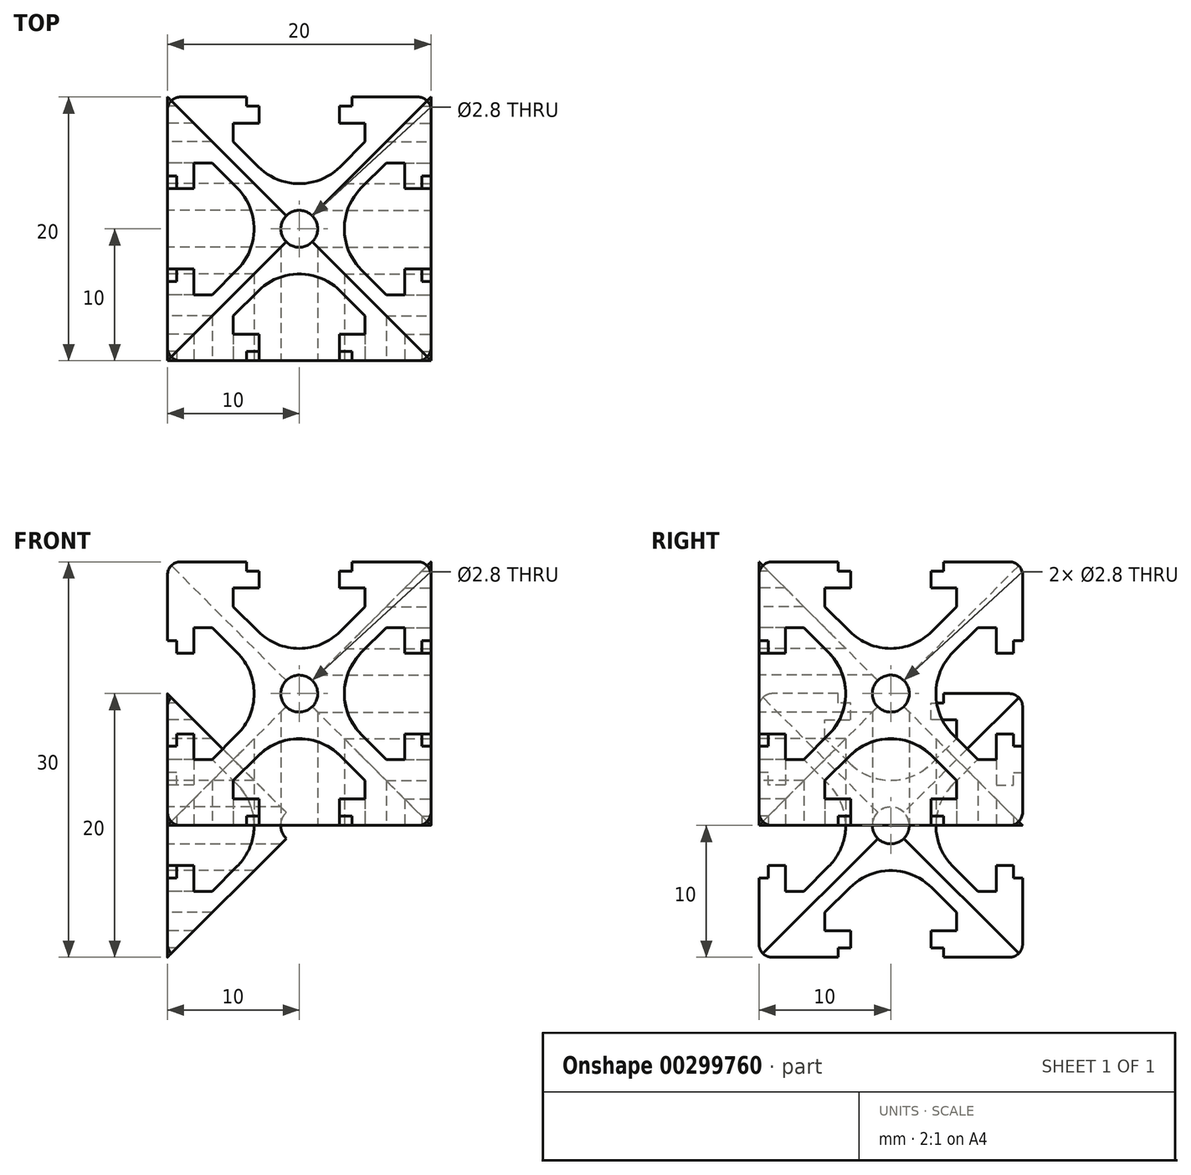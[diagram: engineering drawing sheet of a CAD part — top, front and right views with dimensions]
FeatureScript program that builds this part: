
annotation { "Feature Type Name" : "Feature", "Feature Type Description" : "" }
export const myFeature = defineFeature(function(context is Context, id is Id, definition is map)
    precondition{}
    {
        {
            var Q0;
            Q0=qCreatedBy(makeId("Top.planeOp"),FACE);
            var sketch = newSketch(context, id + "F0", { "sketchPlane" : qUnion([Q0])});
            skLineSegment(sketch, "E0.7", {"start": v(-3.11, 4.71) * mm, "end": v(-5, 6.6) * mm});
            skLineSegment(sketch, "E1.0", {"start": v(-5, 6.6) * mm, "end": v(-5, 8) * mm});
            skLineSegment(sketch, "E2.0", {"start": v(-5, 8) * mm, "end": v(-3.05, 8) * mm});
            skLineSegment(sketch, "E3.0", {"start": v(-3.05, 8) * mm, "end": v(-3.05, 9.3) * mm});
            skLineSegment(sketch, "E4.0", {"start": v(-3.05, 9.3) * mm, "end": v(-4, 9.3) * mm});
            skLineSegment(sketch, "E5.0", {"start": v(-4, 9.3) * mm, "end": v(-4, 10) * mm});
            skLineSegment(sketch, "E6.0", {"start": v(-4, 10) * mm, "end": v(-9, 10) * mm});
            skArc(sketch, "E7.0", {"start": v(-9, 10) * mm, "mid": v(-9.7, 9.7) * mm, "end": v(-10, 9) * mm});
            skCircle(sketch, "E8.0", {"center": v(0, 0) * mm, "radius": 1.4 * mm});
            skLineSegment(sketch, "E9", {"start": v(0, 0) * mm, "end": v(0, 10) * mm, "construction": true});
            skLineSegment(sketch, "E10", {"start": v(0, 0) * mm, "end": v(-9.7, 9.7) * mm, "construction": true});
            skArc(sketch, "E11", {"start": v(-3.11, 4.71) * mm, "mid": v(0, 3.42) * mm, "end": v(3.11, 4.71) * mm});
            skLineSegment(sketch, "E12.MirrorCS", {"start": v(-6.6, 5) * mm, "end": v(-8, 5) * mm});
            skLineSegment(sketch, "E13.MirrorCS", {"start": v(-8, 5) * mm, "end": v(-8, 3.05) * mm});
            skLineSegment(sketch, "E14.MirrorCS", {"start": v(-8, 3.05) * mm, "end": v(-9.3, 3.05) * mm});
            skLineSegment(sketch, "E15.MirrorCS", {"start": v(-9.3, 3.05) * mm, "end": v(-9.3, 4) * mm});
            skLineSegment(sketch, "E16.MirrorCS", {"start": v(-10, 4) * mm, "end": v(-10, 9) * mm});
            skLineSegment(sketch, "E17.MirrorCS", {"start": v(-9.3, 4) * mm, "end": v(-10, 4) * mm});
            skLineSegment(sketch, "E18.MirrorCS", {"start": v(-4.71, 3.11) * mm, "end": v(-6.6, 5) * mm});
            skLineSegment(sketch, "E19.1.0", {"start": v(-8, -3.05) * mm, "end": v(-9.3, -3.05) * mm});
            skLineSegment(sketch, "E19.1.1", {"start": v(-3.05, -8) * mm, "end": v(-3.05, -9.3) * mm});
            skLineSegment(sketch, "E19.1.2", {"start": v(-8, -5) * mm, "end": v(-8, -3.05) * mm});
            skLineSegment(sketch, "E19.1.3", {"start": v(-4.71, -3.11) * mm, "end": v(-6.6, -5) * mm});
            skLineSegment(sketch, "E19.1.4", {"start": v(-5, -8) * mm, "end": v(-3.05, -8) * mm});
            skArc(sketch, "E19.1.5", {"start": v(-4.71, -3.11) * mm, "mid": v(-3.42, 0) * mm, "end": v(-4.71, 3.11) * mm});
            skLineSegment(sketch, "E19.1.6", {"start": v(-10, -4) * mm, "end": v(-10, -9) * mm});
            skLineSegment(sketch, "E19.1.7", {"start": v(-3.11, -4.71) * mm, "end": v(-5, -6.6) * mm});
            skLineSegment(sketch, "E19.1.8", {"start": v(-5, -6.6) * mm, "end": v(-5, -8) * mm});
            skLineSegment(sketch, "E19.1.9", {"start": v(-4, -10) * mm, "end": v(-9, -10) * mm});
            skLineSegment(sketch, "E19.1.10", {"start": v(-6.6, -5) * mm, "end": v(-8, -5) * mm});
            skArc(sketch, "E19.1.11", {"start": v(-10, -9) * mm, "mid": v(-9.7, -9.7) * mm, "end": v(-9, -10) * mm});
            skLineSegment(sketch, "E19.1.12", {"start": v(-9.3, -4) * mm, "end": v(-10, -4) * mm});
            skLineSegment(sketch, "E19.1.13", {"start": v(-4, -9.3) * mm, "end": v(-4, -10) * mm});
            skLineSegment(sketch, "E19.1.14", {"start": v(-9.3, -3.05) * mm, "end": v(-9.3, -4) * mm});
            skLineSegment(sketch, "E19.1.15", {"start": v(-3.05, -9.3) * mm, "end": v(-4, -9.3) * mm});
            skLineSegment(sketch, "E19.2.0", {"start": v(3.05, -8) * mm, "end": v(3.05, -9.3) * mm});
            skLineSegment(sketch, "E19.2.1", {"start": v(8, -3.05) * mm, "end": v(9.3, -3.05) * mm});
            skLineSegment(sketch, "E19.2.2", {"start": v(5, -8) * mm, "end": v(3.05, -8) * mm});
            skLineSegment(sketch, "E19.2.3", {"start": v(3.11, -4.71) * mm, "end": v(5, -6.6) * mm});
            skLineSegment(sketch, "E19.2.4", {"start": v(8, -5) * mm, "end": v(8, -3.05) * mm});
            skArc(sketch, "E19.2.5", {"start": v(3.11, -4.71) * mm, "mid": v(0, -3.42) * mm, "end": v(-3.11, -4.71) * mm});
            skLineSegment(sketch, "E19.2.6", {"start": v(4, -10) * mm, "end": v(9, -10) * mm});
            skLineSegment(sketch, "E19.2.7", {"start": v(4.71, -3.11) * mm, "end": v(6.6, -5) * mm});
            skLineSegment(sketch, "E19.2.8", {"start": v(6.6, -5) * mm, "end": v(8, -5) * mm});
            skLineSegment(sketch, "E19.2.9", {"start": v(10, -4) * mm, "end": v(10, -9) * mm});
            skLineSegment(sketch, "E19.2.10", {"start": v(5, -6.6) * mm, "end": v(5, -8) * mm});
            skArc(sketch, "E19.2.11", {"start": v(9, -10) * mm, "mid": v(9.7, -9.7) * mm, "end": v(10, -9) * mm});
            skLineSegment(sketch, "E19.2.12", {"start": v(4, -9.3) * mm, "end": v(4, -10) * mm});
            skLineSegment(sketch, "E19.2.13", {"start": v(9.3, -4) * mm, "end": v(10, -4) * mm});
            skLineSegment(sketch, "E19.2.14", {"start": v(3.05, -9.3) * mm, "end": v(4, -9.3) * mm});
            skLineSegment(sketch, "E19.2.15", {"start": v(9.3, -3.05) * mm, "end": v(9.3, -4) * mm});
            skLineSegment(sketch, "E19.3.0", {"start": v(8, 3.05) * mm, "end": v(9.3, 3.05) * mm});
            skLineSegment(sketch, "E19.3.1", {"start": v(3.05, 8) * mm, "end": v(3.05, 9.3) * mm});
            skLineSegment(sketch, "E19.3.2", {"start": v(8, 5) * mm, "end": v(8, 3.05) * mm});
            skLineSegment(sketch, "E19.3.3", {"start": v(4.71, 3.11) * mm, "end": v(6.6, 5) * mm});
            skLineSegment(sketch, "E19.3.4", {"start": v(5, 8) * mm, "end": v(3.05, 8) * mm});
            skArc(sketch, "E19.3.5", {"start": v(4.71, 3.11) * mm, "mid": v(3.42, 0) * mm, "end": v(4.71, -3.11) * mm});
            skLineSegment(sketch, "E19.3.6", {"start": v(10, 4) * mm, "end": v(10, 9) * mm});
            skLineSegment(sketch, "E19.3.7", {"start": v(3.11, 4.71) * mm, "end": v(5, 6.6) * mm});
            skLineSegment(sketch, "E19.3.8", {"start": v(5, 6.6) * mm, "end": v(5, 8) * mm});
            skLineSegment(sketch, "E19.3.9", {"start": v(4, 10) * mm, "end": v(9, 10) * mm});
            skLineSegment(sketch, "E19.3.10", {"start": v(6.6, 5) * mm, "end": v(8, 5) * mm});
            skArc(sketch, "E19.3.11", {"start": v(10, 9) * mm, "mid": v(9.7, 9.7) * mm, "end": v(9, 10) * mm});
            skLineSegment(sketch, "E19.3.12", {"start": v(9.3, 4) * mm, "end": v(10, 4) * mm});
            skLineSegment(sketch, "E19.3.13", {"start": v(4, 9.3) * mm, "end": v(4, 10) * mm});
            skLineSegment(sketch, "E19.3.14", {"start": v(9.3, 3.05) * mm, "end": v(9.3, 4) * mm});
            skLineSegment(sketch, "E19.3.15", {"start": v(3.05, 9.3) * mm, "end": v(4, 9.3) * mm});
            skLineSegment(sketch, "E20", {"start": v(0, 0) * mm, "end": v(-10, 0) * mm, "construction": true});
            skSolve(sketch);
        }
        {
            var Q0;
            Q0=makeQuery(id+"F0.imprint","IMPRINT",FACE,{"disambiguationData":[TD([[makeQuery(id+"F0.imprint","IMPRINT",EDGE,{"derivedFrom":sQuery(id+"F0.wireOp",EDGE,"E0.7")}),1.0]])]});
            extrude(context, id + "F1", {"entities" : qUnion([Q0]), "depth" : 10 * mm});
        }
        {
            var Q0;
            Q0=qCreatedBy(makeId("Top.planeOp"),FACE);
            var sketch = newSketch(context, id + "F2", { "sketchPlane" : qUnion([Q0])});
            skLineSegment(sketch, "E21.bottom", {"start": v(-10, 10) * mm, "end": v(10, 10) * mm});
            skLineSegment(sketch, "E21.top", {"start": v(-10, -10) * mm, "end": v(10, -10) * mm});
            skLineSegment(sketch, "E21.left", {"start": v(-10, 10) * mm, "end": v(-10, -10) * mm});
            skLineSegment(sketch, "E21.right", {"start": v(10, 10) * mm, "end": v(10, -10) * mm});
            skPoint(sketch, "E21.middle", {"position": v(0, 0) * mm});
            skSolve(sketch);
        }
        {
            var Q0;
            Q0=makeQuery(id+"F2.imprint","IMPRINT",FACE,{"disambiguationData":[TD([[makeQuery(id+"F2.imprint","IMPRINT",EDGE,{"derivedFrom":sQuery(id+"F2.wireOp",EDGE,"E21.bottom")}),-1.0]])]});
            extrude(context, id + "F3", {"entities" : qUnion([Q0]), "depth" : 10 * mm, "hasDraft" : true, "draftAngle" : 45 * degree, "draftPullDirection" : true});
        }
        {
            var Q0;
            Q0=makeQuery(id+"F1.opExtrude","SWEPT_BODY",BODY,{"disambiguationData":[OSD([sQuery(id+"F0.wireOp",EDGE,"E0.7"),sQuery(id+"F0.wireOp",EDGE,"E1.0"),sQuery(id+"F0.wireOp",EDGE,"E2.0"),sQuery(id+"F0.wireOp",EDGE,"E3.0"),sQuery(id+"F0.wireOp",EDGE,"E4.0"),sQuery(id+"F0.wireOp",EDGE,"E5.0"),sQuery(id+"F0.wireOp",EDGE,"E6.0"),sQuery(id+"F0.wireOp",EDGE,"E7.0"),sQuery(id+"F0.wireOp",EDGE,"E8.0"),sQuery(id+"F0.wireOp",EDGE,"E11"),sQuery(id+"F0.wireOp",EDGE,"E12.MirrorCS"),sQuery(id+"F0.wireOp",EDGE,"E13.MirrorCS"),sQuery(id+"F0.wireOp",EDGE,"E14.MirrorCS"),sQuery(id+"F0.wireOp",EDGE,"E15.MirrorCS"),sQuery(id+"F0.wireOp",EDGE,"E16.MirrorCS"),sQuery(id+"F0.wireOp",EDGE,"E17.MirrorCS"),sQuery(id+"F0.wireOp",EDGE,"E18.MirrorCS"),sQuery(id+"F0.wireOp",EDGE,"E19.1.0"),sQuery(id+"F0.wireOp",EDGE,"E19.1.1"),sQuery(id+"F0.wireOp",EDGE,"E19.1.2"),sQuery(id+"F0.wireOp",EDGE,"E19.1.3"),sQuery(id+"F0.wireOp",EDGE,"E19.1.4"),sQuery(id+"F0.wireOp",EDGE,"E19.1.5"),sQuery(id+"F0.wireOp",EDGE,"E19.1.6"),sQuery(id+"F0.wireOp",EDGE,"E19.1.7"),sQuery(id+"F0.wireOp",EDGE,"E19.1.8"),sQuery(id+"F0.wireOp",EDGE,"E19.1.9"),sQuery(id+"F0.wireOp",EDGE,"E19.1.10"),sQuery(id+"F0.wireOp",EDGE,"E19.1.11"),sQuery(id+"F0.wireOp",EDGE,"E19.1.12"),sQuery(id+"F0.wireOp",EDGE,"E19.1.13"),sQuery(id+"F0.wireOp",EDGE,"E19.1.14"),sQuery(id+"F0.wireOp",EDGE,"E19.1.15"),sQuery(id+"F0.wireOp",EDGE,"E19.2.0"),sQuery(id+"F0.wireOp",EDGE,"E19.2.1"),sQuery(id+"F0.wireOp",EDGE,"E19.2.2"),sQuery(id+"F0.wireOp",EDGE,"E19.2.3"),sQuery(id+"F0.wireOp",EDGE,"E19.2.4"),sQuery(id+"F0.wireOp",EDGE,"E19.2.5"),sQuery(id+"F0.wireOp",EDGE,"E19.2.6"),sQuery(id+"F0.wireOp",EDGE,"E19.2.7"),sQuery(id+"F0.wireOp",EDGE,"E19.2.8"),sQuery(id+"F0.wireOp",EDGE,"E19.2.9"),sQuery(id+"F0.wireOp",EDGE,"E19.2.10"),sQuery(id+"F0.wireOp",EDGE,"E19.2.11"),sQuery(id+"F0.wireOp",EDGE,"E19.2.12"),sQuery(id+"F0.wireOp",EDGE,"E19.2.13"),sQuery(id+"F0.wireOp",EDGE,"E19.2.14"),sQuery(id+"F0.wireOp",EDGE,"E19.2.15"),sQuery(id+"F0.wireOp",EDGE,"E19.3.0"),sQuery(id+"F0.wireOp",EDGE,"E19.3.1"),sQuery(id+"F0.wireOp",EDGE,"E19.3.2"),sQuery(id+"F0.wireOp",EDGE,"E19.3.3"),sQuery(id+"F0.wireOp",EDGE,"E19.3.4"),sQuery(id+"F0.wireOp",EDGE,"E19.3.5"),sQuery(id+"F0.wireOp",EDGE,"E19.3.6"),sQuery(id+"F0.wireOp",EDGE,"E19.3.7"),sQuery(id+"F0.wireOp",EDGE,"E19.3.8"),sQuery(id+"F0.wireOp",EDGE,"E19.3.9"),sQuery(id+"F0.wireOp",EDGE,"E19.3.10"),sQuery(id+"F0.wireOp",EDGE,"E19.3.11"),sQuery(id+"F0.wireOp",EDGE,"E19.3.12"),sQuery(id+"F0.wireOp",EDGE,"E19.3.13"),sQuery(id+"F0.wireOp",EDGE,"E19.3.14"),sQuery(id+"F0.wireOp",EDGE,"E19.3.15")])]});
            var Q1;
            Q1=makeQuery(id+"F3.opExtrude","SWEPT_BODY",BODY,{"disambiguationData":[OSD([sQuery(id+"F2.wireOp",EDGE,"E21.bottom"),sQuery(id+"F2.wireOp",EDGE,"E21.top"),sQuery(id+"F2.wireOp",EDGE,"E21.left"),sQuery(id+"F2.wireOp",EDGE,"E21.right")])]});
            booleanBodies(context, id + "F4", {"operationType" : BooleanOperationType.INTERSECTION, "tools" : qUnion([Q0, Q1])});
        }
        {
            var Q0;
            Q0=makeQuery(id+"F4.opBoolean","INTERSECT",BODY,{"derivedFrom":[makeQuery(id+"F1.opExtrude","SWEPT_BODY",BODY,{"disambiguationData":[OSD([sQuery(id+"F0.wireOp",EDGE,"E0.7"),sQuery(id+"F0.wireOp",EDGE,"E1.0"),sQuery(id+"F0.wireOp",EDGE,"E2.0"),sQuery(id+"F0.wireOp",EDGE,"E3.0"),sQuery(id+"F0.wireOp",EDGE,"E4.0"),sQuery(id+"F0.wireOp",EDGE,"E5.0"),sQuery(id+"F0.wireOp",EDGE,"E6.0"),sQuery(id+"F0.wireOp",EDGE,"E7.0"),sQuery(id+"F0.wireOp",EDGE,"E8.0"),sQuery(id+"F0.wireOp",EDGE,"E11"),sQuery(id+"F0.wireOp",EDGE,"E12.MirrorCS"),sQuery(id+"F0.wireOp",EDGE,"E13.MirrorCS"),sQuery(id+"F0.wireOp",EDGE,"E14.MirrorCS"),sQuery(id+"F0.wireOp",EDGE,"E15.MirrorCS"),sQuery(id+"F0.wireOp",EDGE,"E16.MirrorCS"),sQuery(id+"F0.wireOp",EDGE,"E17.MirrorCS"),sQuery(id+"F0.wireOp",EDGE,"E18.MirrorCS"),sQuery(id+"F0.wireOp",EDGE,"E19.1.0"),sQuery(id+"F0.wireOp",EDGE,"E19.1.1"),sQuery(id+"F0.wireOp",EDGE,"E19.1.2"),sQuery(id+"F0.wireOp",EDGE,"E19.1.3"),sQuery(id+"F0.wireOp",EDGE,"E19.1.4"),sQuery(id+"F0.wireOp",EDGE,"E19.1.5"),sQuery(id+"F0.wireOp",EDGE,"E19.1.6"),sQuery(id+"F0.wireOp",EDGE,"E19.1.7"),sQuery(id+"F0.wireOp",EDGE,"E19.1.8"),sQuery(id+"F0.wireOp",EDGE,"E19.1.9"),sQuery(id+"F0.wireOp",EDGE,"E19.1.10"),sQuery(id+"F0.wireOp",EDGE,"E19.1.11"),sQuery(id+"F0.wireOp",EDGE,"E19.1.12"),sQuery(id+"F0.wireOp",EDGE,"E19.1.13"),sQuery(id+"F0.wireOp",EDGE,"E19.1.14"),sQuery(id+"F0.wireOp",EDGE,"E19.1.15"),sQuery(id+"F0.wireOp",EDGE,"E19.2.0"),sQuery(id+"F0.wireOp",EDGE,"E19.2.1"),sQuery(id+"F0.wireOp",EDGE,"E19.2.2"),sQuery(id+"F0.wireOp",EDGE,"E19.2.3"),sQuery(id+"F0.wireOp",EDGE,"E19.2.4"),sQuery(id+"F0.wireOp",EDGE,"E19.2.5"),sQuery(id+"F0.wireOp",EDGE,"E19.2.6"),sQuery(id+"F0.wireOp",EDGE,"E19.2.7"),sQuery(id+"F0.wireOp",EDGE,"E19.2.8"),sQuery(id+"F0.wireOp",EDGE,"E19.2.9"),sQuery(id+"F0.wireOp",EDGE,"E19.2.10"),sQuery(id+"F0.wireOp",EDGE,"E19.2.11"),sQuery(id+"F0.wireOp",EDGE,"E19.2.12"),sQuery(id+"F0.wireOp",EDGE,"E19.2.13"),sQuery(id+"F0.wireOp",EDGE,"E19.2.14"),sQuery(id+"F0.wireOp",EDGE,"E19.2.15"),sQuery(id+"F0.wireOp",EDGE,"E19.3.0"),sQuery(id+"F0.wireOp",EDGE,"E19.3.1"),sQuery(id+"F0.wireOp",EDGE,"E19.3.2"),sQuery(id+"F0.wireOp",EDGE,"E19.3.3"),sQuery(id+"F0.wireOp",EDGE,"E19.3.4"),sQuery(id+"F0.wireOp",EDGE,"E19.3.5"),sQuery(id+"F0.wireOp",EDGE,"E19.3.6"),sQuery(id+"F0.wireOp",EDGE,"E19.3.7"),sQuery(id+"F0.wireOp",EDGE,"E19.3.8"),sQuery(id+"F0.wireOp",EDGE,"E19.3.9"),sQuery(id+"F0.wireOp",EDGE,"E19.3.10"),sQuery(id+"F0.wireOp",EDGE,"E19.3.11"),sQuery(id+"F0.wireOp",EDGE,"E19.3.12"),sQuery(id+"F0.wireOp",EDGE,"E19.3.13"),sQuery(id+"F0.wireOp",EDGE,"E19.3.14"),sQuery(id+"F0.wireOp",EDGE,"E19.3.15")])]}),makeQuery(id+"F3.opExtrude","SWEPT_BODY",BODY,{"disambiguationData":[OSD([sQuery(id+"F2.wireOp",EDGE,"E21.bottom"),sQuery(id+"F2.wireOp",EDGE,"E21.top"),sQuery(id+"F2.wireOp",EDGE,"E21.left"),sQuery(id+"F2.wireOp",EDGE,"E21.right")])]})]});
            var Q1;
            Q1=sQuery(id+"F0.wireOp",EDGE,"E9");
            transform(context, id + "F5", {"entities" : qUnion([Q0]), "transformType" : TransformType.ROTATION, "transformAxis" : qUnion([Q1]), "angle" : 90 * degree, "makeCopy" : true});
        }
        {
            var Q0;
            Q0=makeQuery(id+"F5.opPattern","COPY",BODY,{"derivedFrom":makeQuery(id+"F4.opBoolean","INTERSECT",BODY,{"derivedFrom":[makeQuery(id+"F1.opExtrude","SWEPT_BODY",BODY,{"disambiguationData":[OSD([sQuery(id+"F0.wireOp",EDGE,"E0.7"),sQuery(id+"F0.wireOp",EDGE,"E1.0"),sQuery(id+"F0.wireOp",EDGE,"E2.0"),sQuery(id+"F0.wireOp",EDGE,"E3.0"),sQuery(id+"F0.wireOp",EDGE,"E4.0"),sQuery(id+"F0.wireOp",EDGE,"E5.0"),sQuery(id+"F0.wireOp",EDGE,"E6.0"),sQuery(id+"F0.wireOp",EDGE,"E7.0"),sQuery(id+"F0.wireOp",EDGE,"E8.0"),sQuery(id+"F0.wireOp",EDGE,"E11"),sQuery(id+"F0.wireOp",EDGE,"E12.MirrorCS"),sQuery(id+"F0.wireOp",EDGE,"E13.MirrorCS"),sQuery(id+"F0.wireOp",EDGE,"E14.MirrorCS"),sQuery(id+"F0.wireOp",EDGE,"E15.MirrorCS"),sQuery(id+"F0.wireOp",EDGE,"E16.MirrorCS"),sQuery(id+"F0.wireOp",EDGE,"E17.MirrorCS"),sQuery(id+"F0.wireOp",EDGE,"E18.MirrorCS"),sQuery(id+"F0.wireOp",EDGE,"E19.1.0"),sQuery(id+"F0.wireOp",EDGE,"E19.1.1"),sQuery(id+"F0.wireOp",EDGE,"E19.1.2"),sQuery(id+"F0.wireOp",EDGE,"E19.1.3"),sQuery(id+"F0.wireOp",EDGE,"E19.1.4"),sQuery(id+"F0.wireOp",EDGE,"E19.1.5"),sQuery(id+"F0.wireOp",EDGE,"E19.1.6"),sQuery(id+"F0.wireOp",EDGE,"E19.1.7"),sQuery(id+"F0.wireOp",EDGE,"E19.1.8"),sQuery(id+"F0.wireOp",EDGE,"E19.1.9"),sQuery(id+"F0.wireOp",EDGE,"E19.1.10"),sQuery(id+"F0.wireOp",EDGE,"E19.1.11"),sQuery(id+"F0.wireOp",EDGE,"E19.1.12"),sQuery(id+"F0.wireOp",EDGE,"E19.1.13"),sQuery(id+"F0.wireOp",EDGE,"E19.1.14"),sQuery(id+"F0.wireOp",EDGE,"E19.1.15"),sQuery(id+"F0.wireOp",EDGE,"E19.2.0"),sQuery(id+"F0.wireOp",EDGE,"E19.2.1"),sQuery(id+"F0.wireOp",EDGE,"E19.2.2"),sQuery(id+"F0.wireOp",EDGE,"E19.2.3"),sQuery(id+"F0.wireOp",EDGE,"E19.2.4"),sQuery(id+"F0.wireOp",EDGE,"E19.2.5"),sQuery(id+"F0.wireOp",EDGE,"E19.2.6"),sQuery(id+"F0.wireOp",EDGE,"E19.2.7"),sQuery(id+"F0.wireOp",EDGE,"E19.2.8"),sQuery(id+"F0.wireOp",EDGE,"E19.2.9"),sQuery(id+"F0.wireOp",EDGE,"E19.2.10"),sQuery(id+"F0.wireOp",EDGE,"E19.2.11"),sQuery(id+"F0.wireOp",EDGE,"E19.2.12"),sQuery(id+"F0.wireOp",EDGE,"E19.2.13"),sQuery(id+"F0.wireOp",EDGE,"E19.2.14"),sQuery(id+"F0.wireOp",EDGE,"E19.2.15"),sQuery(id+"F0.wireOp",EDGE,"E19.3.0"),sQuery(id+"F0.wireOp",EDGE,"E19.3.1"),sQuery(id+"F0.wireOp",EDGE,"E19.3.2"),sQuery(id+"F0.wireOp",EDGE,"E19.3.3"),sQuery(id+"F0.wireOp",EDGE,"E19.3.4"),sQuery(id+"F0.wireOp",EDGE,"E19.3.5"),sQuery(id+"F0.wireOp",EDGE,"E19.3.6"),sQuery(id+"F0.wireOp",EDGE,"E19.3.7"),sQuery(id+"F0.wireOp",EDGE,"E19.3.8"),sQuery(id+"F0.wireOp",EDGE,"E19.3.9"),sQuery(id+"F0.wireOp",EDGE,"E19.3.10"),sQuery(id+"F0.wireOp",EDGE,"E19.3.11"),sQuery(id+"F0.wireOp",EDGE,"E19.3.12"),sQuery(id+"F0.wireOp",EDGE,"E19.3.13"),sQuery(id+"F0.wireOp",EDGE,"E19.3.14"),sQuery(id+"F0.wireOp",EDGE,"E19.3.15")])]}),makeQuery(id+"F3.opExtrude","SWEPT_BODY",BODY,{"disambiguationData":[OSD([sQuery(id+"F2.wireOp",EDGE,"E21.bottom"),sQuery(id+"F2.wireOp",EDGE,"E21.top"),sQuery(id+"F2.wireOp",EDGE,"E21.left"),sQuery(id+"F2.wireOp",EDGE,"E21.right")])]})]}),"instanceName":"1"});
            transform(context, id + "F6", {"entities" : qUnion([Q0]), "transformType" : TransformType.TRANSLATION_3D, "dx" : -10 * mm, "dy" : 0 * mm, "dz" : 10 * mm, "makeCopy" : false});
        }
        {
            var Q0;
            Q0=makeQuery(id+"F4.opBoolean","INTERSECT",BODY,{"derivedFrom":[makeQuery(id+"F1.opExtrude","SWEPT_BODY",BODY,{"disambiguationData":[OSD([sQuery(id+"F0.wireOp",EDGE,"E0.7"),sQuery(id+"F0.wireOp",EDGE,"E1.0"),sQuery(id+"F0.wireOp",EDGE,"E2.0"),sQuery(id+"F0.wireOp",EDGE,"E3.0"),sQuery(id+"F0.wireOp",EDGE,"E4.0"),sQuery(id+"F0.wireOp",EDGE,"E5.0"),sQuery(id+"F0.wireOp",EDGE,"E6.0"),sQuery(id+"F0.wireOp",EDGE,"E7.0"),sQuery(id+"F0.wireOp",EDGE,"E8.0"),sQuery(id+"F0.wireOp",EDGE,"E11"),sQuery(id+"F0.wireOp",EDGE,"E12.MirrorCS"),sQuery(id+"F0.wireOp",EDGE,"E13.MirrorCS"),sQuery(id+"F0.wireOp",EDGE,"E14.MirrorCS"),sQuery(id+"F0.wireOp",EDGE,"E15.MirrorCS"),sQuery(id+"F0.wireOp",EDGE,"E16.MirrorCS"),sQuery(id+"F0.wireOp",EDGE,"E17.MirrorCS"),sQuery(id+"F0.wireOp",EDGE,"E18.MirrorCS"),sQuery(id+"F0.wireOp",EDGE,"E19.1.0"),sQuery(id+"F0.wireOp",EDGE,"E19.1.1"),sQuery(id+"F0.wireOp",EDGE,"E19.1.2"),sQuery(id+"F0.wireOp",EDGE,"E19.1.3"),sQuery(id+"F0.wireOp",EDGE,"E19.1.4"),sQuery(id+"F0.wireOp",EDGE,"E19.1.5"),sQuery(id+"F0.wireOp",EDGE,"E19.1.6"),sQuery(id+"F0.wireOp",EDGE,"E19.1.7"),sQuery(id+"F0.wireOp",EDGE,"E19.1.8"),sQuery(id+"F0.wireOp",EDGE,"E19.1.9"),sQuery(id+"F0.wireOp",EDGE,"E19.1.10"),sQuery(id+"F0.wireOp",EDGE,"E19.1.11"),sQuery(id+"F0.wireOp",EDGE,"E19.1.12"),sQuery(id+"F0.wireOp",EDGE,"E19.1.13"),sQuery(id+"F0.wireOp",EDGE,"E19.1.14"),sQuery(id+"F0.wireOp",EDGE,"E19.1.15"),sQuery(id+"F0.wireOp",EDGE,"E19.2.0"),sQuery(id+"F0.wireOp",EDGE,"E19.2.1"),sQuery(id+"F0.wireOp",EDGE,"E19.2.2"),sQuery(id+"F0.wireOp",EDGE,"E19.2.3"),sQuery(id+"F0.wireOp",EDGE,"E19.2.4"),sQuery(id+"F0.wireOp",EDGE,"E19.2.5"),sQuery(id+"F0.wireOp",EDGE,"E19.2.6"),sQuery(id+"F0.wireOp",EDGE,"E19.2.7"),sQuery(id+"F0.wireOp",EDGE,"E19.2.8"),sQuery(id+"F0.wireOp",EDGE,"E19.2.9"),sQuery(id+"F0.wireOp",EDGE,"E19.2.10"),sQuery(id+"F0.wireOp",EDGE,"E19.2.11"),sQuery(id+"F0.wireOp",EDGE,"E19.2.12"),sQuery(id+"F0.wireOp",EDGE,"E19.2.13"),sQuery(id+"F0.wireOp",EDGE,"E19.2.14"),sQuery(id+"F0.wireOp",EDGE,"E19.2.15"),sQuery(id+"F0.wireOp",EDGE,"E19.3.0"),sQuery(id+"F0.wireOp",EDGE,"E19.3.1"),sQuery(id+"F0.wireOp",EDGE,"E19.3.2"),sQuery(id+"F0.wireOp",EDGE,"E19.3.3"),sQuery(id+"F0.wireOp",EDGE,"E19.3.4"),sQuery(id+"F0.wireOp",EDGE,"E19.3.5"),sQuery(id+"F0.wireOp",EDGE,"E19.3.6"),sQuery(id+"F0.wireOp",EDGE,"E19.3.7"),sQuery(id+"F0.wireOp",EDGE,"E19.3.8"),sQuery(id+"F0.wireOp",EDGE,"E19.3.9"),sQuery(id+"F0.wireOp",EDGE,"E19.3.10"),sQuery(id+"F0.wireOp",EDGE,"E19.3.11"),sQuery(id+"F0.wireOp",EDGE,"E19.3.12"),sQuery(id+"F0.wireOp",EDGE,"E19.3.13"),sQuery(id+"F0.wireOp",EDGE,"E19.3.14"),sQuery(id+"F0.wireOp",EDGE,"E19.3.15")])]}),makeQuery(id+"F3.opExtrude","SWEPT_BODY",BODY,{"disambiguationData":[OSD([sQuery(id+"F2.wireOp",EDGE,"E21.bottom"),sQuery(id+"F2.wireOp",EDGE,"E21.top"),sQuery(id+"F2.wireOp",EDGE,"E21.left"),sQuery(id+"F2.wireOp",EDGE,"E21.right")])]})]});
            var Q1;
            Q1=sQuery(id+"F0.wireOp",EDGE,"E20");
            transform(context, id + "F7", {"entities" : qUnion([Q0]), "transformType" : TransformType.ROTATION, "transformAxis" : qUnion([Q1]), "angle" : 90 * degree, "makeCopy" : true});
        }
        {
            var Q0;
            Q0=makeQuery(id+"F7.opPattern","COPY",BODY,{"derivedFrom":makeQuery(id+"F4.opBoolean","INTERSECT",BODY,{"derivedFrom":[makeQuery(id+"F1.opExtrude","SWEPT_BODY",BODY,{"disambiguationData":[OSD([sQuery(id+"F0.wireOp",EDGE,"E0.7"),sQuery(id+"F0.wireOp",EDGE,"E1.0"),sQuery(id+"F0.wireOp",EDGE,"E2.0"),sQuery(id+"F0.wireOp",EDGE,"E3.0"),sQuery(id+"F0.wireOp",EDGE,"E4.0"),sQuery(id+"F0.wireOp",EDGE,"E5.0"),sQuery(id+"F0.wireOp",EDGE,"E6.0"),sQuery(id+"F0.wireOp",EDGE,"E7.0"),sQuery(id+"F0.wireOp",EDGE,"E8.0"),sQuery(id+"F0.wireOp",EDGE,"E11"),sQuery(id+"F0.wireOp",EDGE,"E12.MirrorCS"),sQuery(id+"F0.wireOp",EDGE,"E13.MirrorCS"),sQuery(id+"F0.wireOp",EDGE,"E14.MirrorCS"),sQuery(id+"F0.wireOp",EDGE,"E15.MirrorCS"),sQuery(id+"F0.wireOp",EDGE,"E16.MirrorCS"),sQuery(id+"F0.wireOp",EDGE,"E17.MirrorCS"),sQuery(id+"F0.wireOp",EDGE,"E18.MirrorCS"),sQuery(id+"F0.wireOp",EDGE,"E19.1.0"),sQuery(id+"F0.wireOp",EDGE,"E19.1.1"),sQuery(id+"F0.wireOp",EDGE,"E19.1.2"),sQuery(id+"F0.wireOp",EDGE,"E19.1.3"),sQuery(id+"F0.wireOp",EDGE,"E19.1.4"),sQuery(id+"F0.wireOp",EDGE,"E19.1.5"),sQuery(id+"F0.wireOp",EDGE,"E19.1.6"),sQuery(id+"F0.wireOp",EDGE,"E19.1.7"),sQuery(id+"F0.wireOp",EDGE,"E19.1.8"),sQuery(id+"F0.wireOp",EDGE,"E19.1.9"),sQuery(id+"F0.wireOp",EDGE,"E19.1.10"),sQuery(id+"F0.wireOp",EDGE,"E19.1.11"),sQuery(id+"F0.wireOp",EDGE,"E19.1.12"),sQuery(id+"F0.wireOp",EDGE,"E19.1.13"),sQuery(id+"F0.wireOp",EDGE,"E19.1.14"),sQuery(id+"F0.wireOp",EDGE,"E19.1.15"),sQuery(id+"F0.wireOp",EDGE,"E19.2.0"),sQuery(id+"F0.wireOp",EDGE,"E19.2.1"),sQuery(id+"F0.wireOp",EDGE,"E19.2.2"),sQuery(id+"F0.wireOp",EDGE,"E19.2.3"),sQuery(id+"F0.wireOp",EDGE,"E19.2.4"),sQuery(id+"F0.wireOp",EDGE,"E19.2.5"),sQuery(id+"F0.wireOp",EDGE,"E19.2.6"),sQuery(id+"F0.wireOp",EDGE,"E19.2.7"),sQuery(id+"F0.wireOp",EDGE,"E19.2.8"),sQuery(id+"F0.wireOp",EDGE,"E19.2.9"),sQuery(id+"F0.wireOp",EDGE,"E19.2.10"),sQuery(id+"F0.wireOp",EDGE,"E19.2.11"),sQuery(id+"F0.wireOp",EDGE,"E19.2.12"),sQuery(id+"F0.wireOp",EDGE,"E19.2.13"),sQuery(id+"F0.wireOp",EDGE,"E19.2.14"),sQuery(id+"F0.wireOp",EDGE,"E19.2.15"),sQuery(id+"F0.wireOp",EDGE,"E19.3.0"),sQuery(id+"F0.wireOp",EDGE,"E19.3.1"),sQuery(id+"F0.wireOp",EDGE,"E19.3.2"),sQuery(id+"F0.wireOp",EDGE,"E19.3.3"),sQuery(id+"F0.wireOp",EDGE,"E19.3.4"),sQuery(id+"F0.wireOp",EDGE,"E19.3.5"),sQuery(id+"F0.wireOp",EDGE,"E19.3.6"),sQuery(id+"F0.wireOp",EDGE,"E19.3.7"),sQuery(id+"F0.wireOp",EDGE,"E19.3.8"),sQuery(id+"F0.wireOp",EDGE,"E19.3.9"),sQuery(id+"F0.wireOp",EDGE,"E19.3.10"),sQuery(id+"F0.wireOp",EDGE,"E19.3.11"),sQuery(id+"F0.wireOp",EDGE,"E19.3.12"),sQuery(id+"F0.wireOp",EDGE,"E19.3.13"),sQuery(id+"F0.wireOp",EDGE,"E19.3.14"),sQuery(id+"F0.wireOp",EDGE,"E19.3.15")])]}),makeQuery(id+"F3.opExtrude","SWEPT_BODY",BODY,{"disambiguationData":[OSD([sQuery(id+"F2.wireOp",EDGE,"E21.bottom"),sQuery(id+"F2.wireOp",EDGE,"E21.top"),sQuery(id+"F2.wireOp",EDGE,"E21.left"),sQuery(id+"F2.wireOp",EDGE,"E21.right")])]})]}),"instanceName":"1"});
            transform(context, id + "F8", {"entities" : qUnion([Q0]), "transformType" : TransformType.TRANSLATION_3D, "dx" : 0 * mm, "dy" : -10 * mm, "dz" : 10 * mm, "makeCopy" : false});
        }
        {
            var Q0;
            Q0=makeQuery(id+"F5.opPattern","COPY",BODY,{"derivedFrom":makeQuery(id+"F4.opBoolean","INTERSECT",BODY,{"derivedFrom":[makeQuery(id+"F1.opExtrude","SWEPT_BODY",BODY,{"disambiguationData":[OSD([sQuery(id+"F0.wireOp",EDGE,"E0.7"),sQuery(id+"F0.wireOp",EDGE,"E1.0"),sQuery(id+"F0.wireOp",EDGE,"E2.0"),sQuery(id+"F0.wireOp",EDGE,"E3.0"),sQuery(id+"F0.wireOp",EDGE,"E4.0"),sQuery(id+"F0.wireOp",EDGE,"E5.0"),sQuery(id+"F0.wireOp",EDGE,"E6.0"),sQuery(id+"F0.wireOp",EDGE,"E7.0"),sQuery(id+"F0.wireOp",EDGE,"E8.0"),sQuery(id+"F0.wireOp",EDGE,"E11"),sQuery(id+"F0.wireOp",EDGE,"E12.MirrorCS"),sQuery(id+"F0.wireOp",EDGE,"E13.MirrorCS"),sQuery(id+"F0.wireOp",EDGE,"E14.MirrorCS"),sQuery(id+"F0.wireOp",EDGE,"E15.MirrorCS"),sQuery(id+"F0.wireOp",EDGE,"E16.MirrorCS"),sQuery(id+"F0.wireOp",EDGE,"E17.MirrorCS"),sQuery(id+"F0.wireOp",EDGE,"E18.MirrorCS"),sQuery(id+"F0.wireOp",EDGE,"E19.1.0"),sQuery(id+"F0.wireOp",EDGE,"E19.1.1"),sQuery(id+"F0.wireOp",EDGE,"E19.1.2"),sQuery(id+"F0.wireOp",EDGE,"E19.1.3"),sQuery(id+"F0.wireOp",EDGE,"E19.1.4"),sQuery(id+"F0.wireOp",EDGE,"E19.1.5"),sQuery(id+"F0.wireOp",EDGE,"E19.1.6"),sQuery(id+"F0.wireOp",EDGE,"E19.1.7"),sQuery(id+"F0.wireOp",EDGE,"E19.1.8"),sQuery(id+"F0.wireOp",EDGE,"E19.1.9"),sQuery(id+"F0.wireOp",EDGE,"E19.1.10"),sQuery(id+"F0.wireOp",EDGE,"E19.1.11"),sQuery(id+"F0.wireOp",EDGE,"E19.1.12"),sQuery(id+"F0.wireOp",EDGE,"E19.1.13"),sQuery(id+"F0.wireOp",EDGE,"E19.1.14"),sQuery(id+"F0.wireOp",EDGE,"E19.1.15"),sQuery(id+"F0.wireOp",EDGE,"E19.2.0"),sQuery(id+"F0.wireOp",EDGE,"E19.2.1"),sQuery(id+"F0.wireOp",EDGE,"E19.2.2"),sQuery(id+"F0.wireOp",EDGE,"E19.2.3"),sQuery(id+"F0.wireOp",EDGE,"E19.2.4"),sQuery(id+"F0.wireOp",EDGE,"E19.2.5"),sQuery(id+"F0.wireOp",EDGE,"E19.2.6"),sQuery(id+"F0.wireOp",EDGE,"E19.2.7"),sQuery(id+"F0.wireOp",EDGE,"E19.2.8"),sQuery(id+"F0.wireOp",EDGE,"E19.2.9"),sQuery(id+"F0.wireOp",EDGE,"E19.2.10"),sQuery(id+"F0.wireOp",EDGE,"E19.2.11"),sQuery(id+"F0.wireOp",EDGE,"E19.2.12"),sQuery(id+"F0.wireOp",EDGE,"E19.2.13"),sQuery(id+"F0.wireOp",EDGE,"E19.2.14"),sQuery(id+"F0.wireOp",EDGE,"E19.2.15"),sQuery(id+"F0.wireOp",EDGE,"E19.3.0"),sQuery(id+"F0.wireOp",EDGE,"E19.3.1"),sQuery(id+"F0.wireOp",EDGE,"E19.3.2"),sQuery(id+"F0.wireOp",EDGE,"E19.3.3"),sQuery(id+"F0.wireOp",EDGE,"E19.3.4"),sQuery(id+"F0.wireOp",EDGE,"E19.3.5"),sQuery(id+"F0.wireOp",EDGE,"E19.3.6"),sQuery(id+"F0.wireOp",EDGE,"E19.3.7"),sQuery(id+"F0.wireOp",EDGE,"E19.3.8"),sQuery(id+"F0.wireOp",EDGE,"E19.3.9"),sQuery(id+"F0.wireOp",EDGE,"E19.3.10"),sQuery(id+"F0.wireOp",EDGE,"E19.3.11"),sQuery(id+"F0.wireOp",EDGE,"E19.3.12"),sQuery(id+"F0.wireOp",EDGE,"E19.3.13"),sQuery(id+"F0.wireOp",EDGE,"E19.3.14"),sQuery(id+"F0.wireOp",EDGE,"E19.3.15")])]}),makeQuery(id+"F3.opExtrude","SWEPT_BODY",BODY,{"disambiguationData":[OSD([sQuery(id+"F2.wireOp",EDGE,"E21.bottom"),sQuery(id+"F2.wireOp",EDGE,"E21.top"),sQuery(id+"F2.wireOp",EDGE,"E21.left"),sQuery(id+"F2.wireOp",EDGE,"E21.right")])]})]}),"instanceName":"1"});
            var Q1;
            Q1=makeQuery(id+"F7.opPattern","COPY",FACE,{"derivedFrom":makeQuery(id+"F1.opExtrude","CAP_FACE",FACE,{"disambiguationData":[OSD([sQuery(id+"F0.wireOp",EDGE,"E0.7"),sQuery(id+"F0.wireOp",EDGE,"E1.0"),sQuery(id+"F0.wireOp",EDGE,"E2.0"),sQuery(id+"F0.wireOp",EDGE,"E3.0"),sQuery(id+"F0.wireOp",EDGE,"E4.0"),sQuery(id+"F0.wireOp",EDGE,"E5.0"),sQuery(id+"F0.wireOp",EDGE,"E6.0"),sQuery(id+"F0.wireOp",EDGE,"E7.0"),sQuery(id+"F0.wireOp",EDGE,"E8.0"),sQuery(id+"F0.wireOp",EDGE,"E11"),sQuery(id+"F0.wireOp",EDGE,"E12.MirrorCS"),sQuery(id+"F0.wireOp",EDGE,"E13.MirrorCS"),sQuery(id+"F0.wireOp",EDGE,"E14.MirrorCS"),sQuery(id+"F0.wireOp",EDGE,"E15.MirrorCS"),sQuery(id+"F0.wireOp",EDGE,"E16.MirrorCS"),sQuery(id+"F0.wireOp",EDGE,"E17.MirrorCS"),sQuery(id+"F0.wireOp",EDGE,"E18.MirrorCS"),sQuery(id+"F0.wireOp",EDGE,"E19.1.0"),sQuery(id+"F0.wireOp",EDGE,"E19.1.1"),sQuery(id+"F0.wireOp",EDGE,"E19.1.2"),sQuery(id+"F0.wireOp",EDGE,"E19.1.3"),sQuery(id+"F0.wireOp",EDGE,"E19.1.4"),sQuery(id+"F0.wireOp",EDGE,"E19.1.5"),sQuery(id+"F0.wireOp",EDGE,"E19.1.6"),sQuery(id+"F0.wireOp",EDGE,"E19.1.7"),sQuery(id+"F0.wireOp",EDGE,"E19.1.8"),sQuery(id+"F0.wireOp",EDGE,"E19.1.9"),sQuery(id+"F0.wireOp",EDGE,"E19.1.10"),sQuery(id+"F0.wireOp",EDGE,"E19.1.11"),sQuery(id+"F0.wireOp",EDGE,"E19.1.12"),sQuery(id+"F0.wireOp",EDGE,"E19.1.13"),sQuery(id+"F0.wireOp",EDGE,"E19.1.14"),sQuery(id+"F0.wireOp",EDGE,"E19.1.15"),sQuery(id+"F0.wireOp",EDGE,"E19.2.0"),sQuery(id+"F0.wireOp",EDGE,"E19.2.1"),sQuery(id+"F0.wireOp",EDGE,"E19.2.2"),sQuery(id+"F0.wireOp",EDGE,"E19.2.3"),sQuery(id+"F0.wireOp",EDGE,"E19.2.4"),sQuery(id+"F0.wireOp",EDGE,"E19.2.5"),sQuery(id+"F0.wireOp",EDGE,"E19.2.6"),sQuery(id+"F0.wireOp",EDGE,"E19.2.7"),sQuery(id+"F0.wireOp",EDGE,"E19.2.8"),sQuery(id+"F0.wireOp",EDGE,"E19.2.9"),sQuery(id+"F0.wireOp",EDGE,"E19.2.10"),sQuery(id+"F0.wireOp",EDGE,"E19.2.11"),sQuery(id+"F0.wireOp",EDGE,"E19.2.12"),sQuery(id+"F0.wireOp",EDGE,"E19.2.13"),sQuery(id+"F0.wireOp",EDGE,"E19.2.14"),sQuery(id+"F0.wireOp",EDGE,"E19.2.15"),sQuery(id+"F0.wireOp",EDGE,"E19.3.0"),sQuery(id+"F0.wireOp",EDGE,"E19.3.1"),sQuery(id+"F0.wireOp",EDGE,"E19.3.2"),sQuery(id+"F0.wireOp",EDGE,"E19.3.3"),sQuery(id+"F0.wireOp",EDGE,"E19.3.4"),sQuery(id+"F0.wireOp",EDGE,"E19.3.5"),sQuery(id+"F0.wireOp",EDGE,"E19.3.6"),sQuery(id+"F0.wireOp",EDGE,"E19.3.7"),sQuery(id+"F0.wireOp",EDGE,"E19.3.8"),sQuery(id+"F0.wireOp",EDGE,"E19.3.9"),sQuery(id+"F0.wireOp",EDGE,"E19.3.10"),sQuery(id+"F0.wireOp",EDGE,"E19.3.11"),sQuery(id+"F0.wireOp",EDGE,"E19.3.12"),sQuery(id+"F0.wireOp",EDGE,"E19.3.13"),sQuery(id+"F0.wireOp",EDGE,"E19.3.14"),sQuery(id+"F0.wireOp",EDGE,"E19.3.15")])],"isStart":true}),"instanceName":"1"});
            mirror(context, id + "F9", {"entities" : qUnion([Q0]), "mirrorPlane" : qUnion([Q1])});
        }
        {
            var Q0;
            Q0=makeQuery(id+"F9.opPattern","COPY",BODY,{"derivedFrom":makeQuery(id+"F5.opPattern","COPY",BODY,{"derivedFrom":makeQuery(id+"F4.opBoolean","INTERSECT",BODY,{"derivedFrom":[makeQuery(id+"F1.opExtrude","SWEPT_BODY",BODY,{"disambiguationData":[OSD([sQuery(id+"F0.wireOp",EDGE,"E0.7"),sQuery(id+"F0.wireOp",EDGE,"E1.0"),sQuery(id+"F0.wireOp",EDGE,"E2.0"),sQuery(id+"F0.wireOp",EDGE,"E3.0"),sQuery(id+"F0.wireOp",EDGE,"E4.0"),sQuery(id+"F0.wireOp",EDGE,"E5.0"),sQuery(id+"F0.wireOp",EDGE,"E6.0"),sQuery(id+"F0.wireOp",EDGE,"E7.0"),sQuery(id+"F0.wireOp",EDGE,"E8.0"),sQuery(id+"F0.wireOp",EDGE,"E11"),sQuery(id+"F0.wireOp",EDGE,"E12.MirrorCS"),sQuery(id+"F0.wireOp",EDGE,"E13.MirrorCS"),sQuery(id+"F0.wireOp",EDGE,"E14.MirrorCS"),sQuery(id+"F0.wireOp",EDGE,"E15.MirrorCS"),sQuery(id+"F0.wireOp",EDGE,"E16.MirrorCS"),sQuery(id+"F0.wireOp",EDGE,"E17.MirrorCS"),sQuery(id+"F0.wireOp",EDGE,"E18.MirrorCS"),sQuery(id+"F0.wireOp",EDGE,"E19.1.0"),sQuery(id+"F0.wireOp",EDGE,"E19.1.1"),sQuery(id+"F0.wireOp",EDGE,"E19.1.2"),sQuery(id+"F0.wireOp",EDGE,"E19.1.3"),sQuery(id+"F0.wireOp",EDGE,"E19.1.4"),sQuery(id+"F0.wireOp",EDGE,"E19.1.5"),sQuery(id+"F0.wireOp",EDGE,"E19.1.6"),sQuery(id+"F0.wireOp",EDGE,"E19.1.7"),sQuery(id+"F0.wireOp",EDGE,"E19.1.8"),sQuery(id+"F0.wireOp",EDGE,"E19.1.9"),sQuery(id+"F0.wireOp",EDGE,"E19.1.10"),sQuery(id+"F0.wireOp",EDGE,"E19.1.11"),sQuery(id+"F0.wireOp",EDGE,"E19.1.12"),sQuery(id+"F0.wireOp",EDGE,"E19.1.13"),sQuery(id+"F0.wireOp",EDGE,"E19.1.14"),sQuery(id+"F0.wireOp",EDGE,"E19.1.15"),sQuery(id+"F0.wireOp",EDGE,"E19.2.0"),sQuery(id+"F0.wireOp",EDGE,"E19.2.1"),sQuery(id+"F0.wireOp",EDGE,"E19.2.2"),sQuery(id+"F0.wireOp",EDGE,"E19.2.3"),sQuery(id+"F0.wireOp",EDGE,"E19.2.4"),sQuery(id+"F0.wireOp",EDGE,"E19.2.5"),sQuery(id+"F0.wireOp",EDGE,"E19.2.6"),sQuery(id+"F0.wireOp",EDGE,"E19.2.7"),sQuery(id+"F0.wireOp",EDGE,"E19.2.8"),sQuery(id+"F0.wireOp",EDGE,"E19.2.9"),sQuery(id+"F0.wireOp",EDGE,"E19.2.10"),sQuery(id+"F0.wireOp",EDGE,"E19.2.11"),sQuery(id+"F0.wireOp",EDGE,"E19.2.12"),sQuery(id+"F0.wireOp",EDGE,"E19.2.13"),sQuery(id+"F0.wireOp",EDGE,"E19.2.14"),sQuery(id+"F0.wireOp",EDGE,"E19.2.15"),sQuery(id+"F0.wireOp",EDGE,"E19.3.0"),sQuery(id+"F0.wireOp",EDGE,"E19.3.1"),sQuery(id+"F0.wireOp",EDGE,"E19.3.2"),sQuery(id+"F0.wireOp",EDGE,"E19.3.3"),sQuery(id+"F0.wireOp",EDGE,"E19.3.4"),sQuery(id+"F0.wireOp",EDGE,"E19.3.5"),sQuery(id+"F0.wireOp",EDGE,"E19.3.6"),sQuery(id+"F0.wireOp",EDGE,"E19.3.7"),sQuery(id+"F0.wireOp",EDGE,"E19.3.8"),sQuery(id+"F0.wireOp",EDGE,"E19.3.9"),sQuery(id+"F0.wireOp",EDGE,"E19.3.10"),sQuery(id+"F0.wireOp",EDGE,"E19.3.11"),sQuery(id+"F0.wireOp",EDGE,"E19.3.12"),sQuery(id+"F0.wireOp",EDGE,"E19.3.13"),sQuery(id+"F0.wireOp",EDGE,"E19.3.14"),sQuery(id+"F0.wireOp",EDGE,"E19.3.15")])]}),makeQuery(id+"F3.opExtrude","SWEPT_BODY",BODY,{"disambiguationData":[OSD([sQuery(id+"F2.wireOp",EDGE,"E21.bottom"),sQuery(id+"F2.wireOp",EDGE,"E21.top"),sQuery(id+"F2.wireOp",EDGE,"E21.left"),sQuery(id+"F2.wireOp",EDGE,"E21.right")])]})]}),"instanceName":"1"}),"instanceName":"1"});
            var Q1;
            Q1=sQuery(id+"F0.wireOp",EDGE,"E9");
            transform(context, id + "F10", {"entities" : qUnion([Q0]), "transformType" : TransformType.ROTATION, "transformAxis" : qUnion([Q1]), "angle" : 180 * degree, "makeCopy" : false});
        }
        {
            var Q0;
            Q0=makeQuery(id+"F9.opPattern","COPY",BODY,{"derivedFrom":makeQuery(id+"F5.opPattern","COPY",BODY,{"derivedFrom":makeQuery(id+"F4.opBoolean","INTERSECT",BODY,{"derivedFrom":[makeQuery(id+"F1.opExtrude","SWEPT_BODY",BODY,{"disambiguationData":[OSD([sQuery(id+"F0.wireOp",EDGE,"E0.7"),sQuery(id+"F0.wireOp",EDGE,"E1.0"),sQuery(id+"F0.wireOp",EDGE,"E2.0"),sQuery(id+"F0.wireOp",EDGE,"E3.0"),sQuery(id+"F0.wireOp",EDGE,"E4.0"),sQuery(id+"F0.wireOp",EDGE,"E5.0"),sQuery(id+"F0.wireOp",EDGE,"E6.0"),sQuery(id+"F0.wireOp",EDGE,"E7.0"),sQuery(id+"F0.wireOp",EDGE,"E8.0"),sQuery(id+"F0.wireOp",EDGE,"E11"),sQuery(id+"F0.wireOp",EDGE,"E12.MirrorCS"),sQuery(id+"F0.wireOp",EDGE,"E13.MirrorCS"),sQuery(id+"F0.wireOp",EDGE,"E14.MirrorCS"),sQuery(id+"F0.wireOp",EDGE,"E15.MirrorCS"),sQuery(id+"F0.wireOp",EDGE,"E16.MirrorCS"),sQuery(id+"F0.wireOp",EDGE,"E17.MirrorCS"),sQuery(id+"F0.wireOp",EDGE,"E18.MirrorCS"),sQuery(id+"F0.wireOp",EDGE,"E19.1.0"),sQuery(id+"F0.wireOp",EDGE,"E19.1.1"),sQuery(id+"F0.wireOp",EDGE,"E19.1.2"),sQuery(id+"F0.wireOp",EDGE,"E19.1.3"),sQuery(id+"F0.wireOp",EDGE,"E19.1.4"),sQuery(id+"F0.wireOp",EDGE,"E19.1.5"),sQuery(id+"F0.wireOp",EDGE,"E19.1.6"),sQuery(id+"F0.wireOp",EDGE,"E19.1.7"),sQuery(id+"F0.wireOp",EDGE,"E19.1.8"),sQuery(id+"F0.wireOp",EDGE,"E19.1.9"),sQuery(id+"F0.wireOp",EDGE,"E19.1.10"),sQuery(id+"F0.wireOp",EDGE,"E19.1.11"),sQuery(id+"F0.wireOp",EDGE,"E19.1.12"),sQuery(id+"F0.wireOp",EDGE,"E19.1.13"),sQuery(id+"F0.wireOp",EDGE,"E19.1.14"),sQuery(id+"F0.wireOp",EDGE,"E19.1.15"),sQuery(id+"F0.wireOp",EDGE,"E19.2.0"),sQuery(id+"F0.wireOp",EDGE,"E19.2.1"),sQuery(id+"F0.wireOp",EDGE,"E19.2.2"),sQuery(id+"F0.wireOp",EDGE,"E19.2.3"),sQuery(id+"F0.wireOp",EDGE,"E19.2.4"),sQuery(id+"F0.wireOp",EDGE,"E19.2.5"),sQuery(id+"F0.wireOp",EDGE,"E19.2.6"),sQuery(id+"F0.wireOp",EDGE,"E19.2.7"),sQuery(id+"F0.wireOp",EDGE,"E19.2.8"),sQuery(id+"F0.wireOp",EDGE,"E19.2.9"),sQuery(id+"F0.wireOp",EDGE,"E19.2.10"),sQuery(id+"F0.wireOp",EDGE,"E19.2.11"),sQuery(id+"F0.wireOp",EDGE,"E19.2.12"),sQuery(id+"F0.wireOp",EDGE,"E19.2.13"),sQuery(id+"F0.wireOp",EDGE,"E19.2.14"),sQuery(id+"F0.wireOp",EDGE,"E19.2.15"),sQuery(id+"F0.wireOp",EDGE,"E19.3.0"),sQuery(id+"F0.wireOp",EDGE,"E19.3.1"),sQuery(id+"F0.wireOp",EDGE,"E19.3.2"),sQuery(id+"F0.wireOp",EDGE,"E19.3.3"),sQuery(id+"F0.wireOp",EDGE,"E19.3.4"),sQuery(id+"F0.wireOp",EDGE,"E19.3.5"),sQuery(id+"F0.wireOp",EDGE,"E19.3.6"),sQuery(id+"F0.wireOp",EDGE,"E19.3.7"),sQuery(id+"F0.wireOp",EDGE,"E19.3.8"),sQuery(id+"F0.wireOp",EDGE,"E19.3.9"),sQuery(id+"F0.wireOp",EDGE,"E19.3.10"),sQuery(id+"F0.wireOp",EDGE,"E19.3.11"),sQuery(id+"F0.wireOp",EDGE,"E19.3.12"),sQuery(id+"F0.wireOp",EDGE,"E19.3.13"),sQuery(id+"F0.wireOp",EDGE,"E19.3.14"),sQuery(id+"F0.wireOp",EDGE,"E19.3.15")])]}),makeQuery(id+"F3.opExtrude","SWEPT_BODY",BODY,{"disambiguationData":[OSD([sQuery(id+"F2.wireOp",EDGE,"E21.bottom"),sQuery(id+"F2.wireOp",EDGE,"E21.top"),sQuery(id+"F2.wireOp",EDGE,"E21.left"),sQuery(id+"F2.wireOp",EDGE,"E21.right")])]})]}),"instanceName":"1"}),"instanceName":"1"});
            transform(context, id + "F11", {"entities" : qUnion([Q0]), "transformType" : TransformType.TRANSLATION_3D, "dx" : 0 * mm, "dy" : 20 * mm, "dz" : 20 * mm, "makeCopy" : false});
        }
        {
            var Q0;
            Q0=makeQuery(id+"F5.opPattern","COPY",BODY,{"derivedFrom":makeQuery(id+"F4.opBoolean","INTERSECT",BODY,{"derivedFrom":[makeQuery(id+"F1.opExtrude","SWEPT_BODY",BODY,{"disambiguationData":[OSD([sQuery(id+"F0.wireOp",EDGE,"E0.7"),sQuery(id+"F0.wireOp",EDGE,"E1.0"),sQuery(id+"F0.wireOp",EDGE,"E2.0"),sQuery(id+"F0.wireOp",EDGE,"E3.0"),sQuery(id+"F0.wireOp",EDGE,"E4.0"),sQuery(id+"F0.wireOp",EDGE,"E5.0"),sQuery(id+"F0.wireOp",EDGE,"E6.0"),sQuery(id+"F0.wireOp",EDGE,"E7.0"),sQuery(id+"F0.wireOp",EDGE,"E8.0"),sQuery(id+"F0.wireOp",EDGE,"E11"),sQuery(id+"F0.wireOp",EDGE,"E12.MirrorCS"),sQuery(id+"F0.wireOp",EDGE,"E13.MirrorCS"),sQuery(id+"F0.wireOp",EDGE,"E14.MirrorCS"),sQuery(id+"F0.wireOp",EDGE,"E15.MirrorCS"),sQuery(id+"F0.wireOp",EDGE,"E16.MirrorCS"),sQuery(id+"F0.wireOp",EDGE,"E17.MirrorCS"),sQuery(id+"F0.wireOp",EDGE,"E18.MirrorCS"),sQuery(id+"F0.wireOp",EDGE,"E19.1.0"),sQuery(id+"F0.wireOp",EDGE,"E19.1.1"),sQuery(id+"F0.wireOp",EDGE,"E19.1.2"),sQuery(id+"F0.wireOp",EDGE,"E19.1.3"),sQuery(id+"F0.wireOp",EDGE,"E19.1.4"),sQuery(id+"F0.wireOp",EDGE,"E19.1.5"),sQuery(id+"F0.wireOp",EDGE,"E19.1.6"),sQuery(id+"F0.wireOp",EDGE,"E19.1.7"),sQuery(id+"F0.wireOp",EDGE,"E19.1.8"),sQuery(id+"F0.wireOp",EDGE,"E19.1.9"),sQuery(id+"F0.wireOp",EDGE,"E19.1.10"),sQuery(id+"F0.wireOp",EDGE,"E19.1.11"),sQuery(id+"F0.wireOp",EDGE,"E19.1.12"),sQuery(id+"F0.wireOp",EDGE,"E19.1.13"),sQuery(id+"F0.wireOp",EDGE,"E19.1.14"),sQuery(id+"F0.wireOp",EDGE,"E19.1.15"),sQuery(id+"F0.wireOp",EDGE,"E19.2.0"),sQuery(id+"F0.wireOp",EDGE,"E19.2.1"),sQuery(id+"F0.wireOp",EDGE,"E19.2.2"),sQuery(id+"F0.wireOp",EDGE,"E19.2.3"),sQuery(id+"F0.wireOp",EDGE,"E19.2.4"),sQuery(id+"F0.wireOp",EDGE,"E19.2.5"),sQuery(id+"F0.wireOp",EDGE,"E19.2.6"),sQuery(id+"F0.wireOp",EDGE,"E19.2.7"),sQuery(id+"F0.wireOp",EDGE,"E19.2.8"),sQuery(id+"F0.wireOp",EDGE,"E19.2.9"),sQuery(id+"F0.wireOp",EDGE,"E19.2.10"),sQuery(id+"F0.wireOp",EDGE,"E19.2.11"),sQuery(id+"F0.wireOp",EDGE,"E19.2.12"),sQuery(id+"F0.wireOp",EDGE,"E19.2.13"),sQuery(id+"F0.wireOp",EDGE,"E19.2.14"),sQuery(id+"F0.wireOp",EDGE,"E19.2.15"),sQuery(id+"F0.wireOp",EDGE,"E19.3.0"),sQuery(id+"F0.wireOp",EDGE,"E19.3.1"),sQuery(id+"F0.wireOp",EDGE,"E19.3.2"),sQuery(id+"F0.wireOp",EDGE,"E19.3.3"),sQuery(id+"F0.wireOp",EDGE,"E19.3.4"),sQuery(id+"F0.wireOp",EDGE,"E19.3.5"),sQuery(id+"F0.wireOp",EDGE,"E19.3.6"),sQuery(id+"F0.wireOp",EDGE,"E19.3.7"),sQuery(id+"F0.wireOp",EDGE,"E19.3.8"),sQuery(id+"F0.wireOp",EDGE,"E19.3.9"),sQuery(id+"F0.wireOp",EDGE,"E19.3.10"),sQuery(id+"F0.wireOp",EDGE,"E19.3.11"),sQuery(id+"F0.wireOp",EDGE,"E19.3.12"),sQuery(id+"F0.wireOp",EDGE,"E19.3.13"),sQuery(id+"F0.wireOp",EDGE,"E19.3.14"),sQuery(id+"F0.wireOp",EDGE,"E19.3.15")])]}),makeQuery(id+"F3.opExtrude","SWEPT_BODY",BODY,{"disambiguationData":[OSD([sQuery(id+"F2.wireOp",EDGE,"E21.bottom"),sQuery(id+"F2.wireOp",EDGE,"E21.top"),sQuery(id+"F2.wireOp",EDGE,"E21.left"),sQuery(id+"F2.wireOp",EDGE,"E21.right")])]})]}),"instanceName":"1"});
            transform(context, id + "F12", {"entities" : qUnion([Q0]), "transformType" : TransformType.TRANSLATION_3D, "dx" : 0 * mm, "dy" : 0 * mm, "dz" : -10 * mm, "makeCopy" : false});
        }
    });
